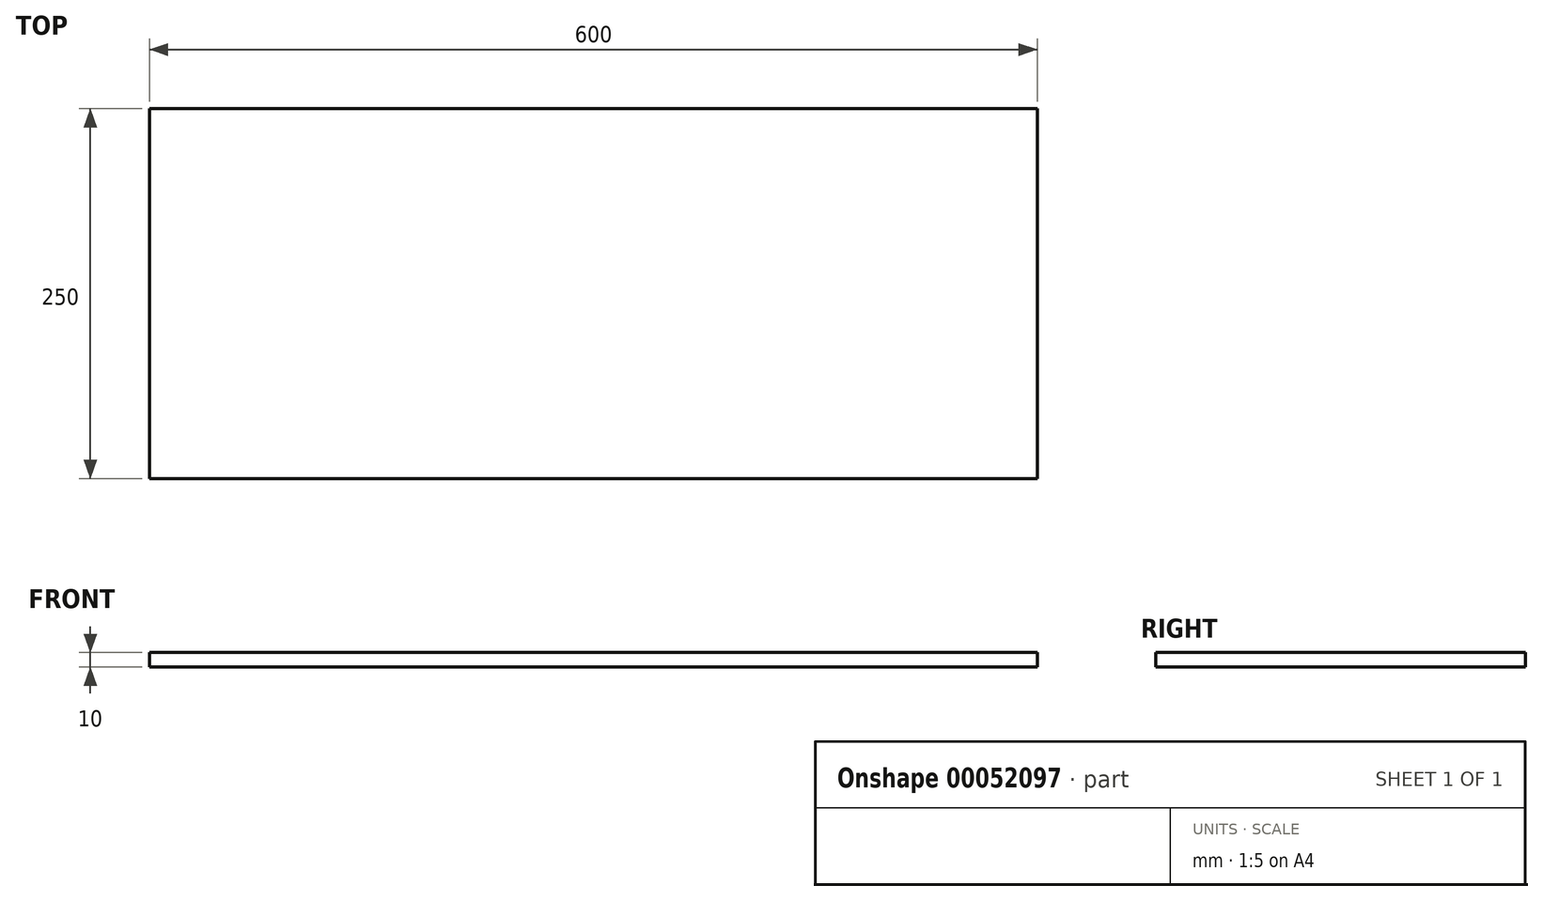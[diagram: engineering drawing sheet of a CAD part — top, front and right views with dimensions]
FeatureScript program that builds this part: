
annotation { "Feature Type Name" : "Feature", "Feature Type Description" : "" }
export const myFeature = defineFeature(function(context is Context, id is Id, definition is map)
    precondition{}
    {
        {
            var Q0;
            Q0=qCreatedBy(makeId("Top.planeOp"),FACE);
            var sketch = newSketch(context, id + "F0", { "sketchPlane" : qUnion([Q0])});
            skLineSegment(sketch, "E0.bottom", {"start": v(0, 0) * mm, "end": v(600, 0) * mm});
            skLineSegment(sketch, "E0.top", {"start": v(0, 250) * mm, "end": v(600, 250) * mm});
            skLineSegment(sketch, "E0.left", {"start": v(0, 0) * mm, "end": v(0, 250) * mm});
            skLineSegment(sketch, "E0.right", {"start": v(600, 0) * mm, "end": v(600, 250) * mm});
            skSolve(sketch);
        }
        {
            var Q0;
            Q0=makeQuery(id+"F0.imprint","IMPRINT",FACE,{"disambiguationData":[TD([[makeQuery(id+"F0.imprint","IMPRINT",EDGE,{"derivedFrom":sQuery(id+"F0.wireOp",EDGE,"E0.bottom")}),1.0]])]});
            extrude(context, id + "F1", {"entities" : qUnion([Q0]), "depth" : 10 * mm});
        }
    });
